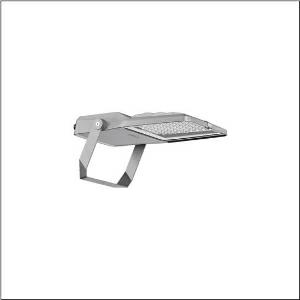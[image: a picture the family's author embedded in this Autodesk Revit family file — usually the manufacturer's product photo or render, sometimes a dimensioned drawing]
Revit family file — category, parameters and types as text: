
# Revit family: floodlight_fl_21_iq_mini___pl52_5xa7772d3d1a_25a1
name_source: partatom
category: Lighting Fixtures
units: mm (PartAtom-declared; Revit-internal decimal feet)

## family parameters
Cut with Voids When Loaded = No
Host = Face
Light Source = No
Part Type = Normal
Room Calculation Point = No
Round Connector Dimension = Use Diameter
Shared = No

## types (1)
- --- (1 x LED, 15340 lm, 143 W, 3000K)
    Apparent Load = 143 VA
    CIE Flux Codes = 26 60 98 100 100
    Color Rendering = 80
    Color Temperature = 3000K
    Default Elevation = 1800 mm
    Description = Floodlight FL 21 iQ mini, floodlight, primary light control with lens, of PMMA, primary optical cover: protective disc, of toughened safety glass, transparent, light distribution: PL52, light emission: direct distribution, installation type: surface-mounted, LED, High Power LED, rated luminous flux: 15.340lm, luminous efficacy: 107lm/W, light colour: 830, colour temperature: 3000K, control gear: iQ Street-Remote/DALI, control: Street-Remote, Auto-Match, Temp-Guard, Night-Set, Smart-Wire, Desk-Remote (wireless, voltage-free reading and setting of iQ features in the workshop via application-optimized NFC function/RFID function), optimised constant luminous flux control (CLO 2.0), with terminal, 6-pole, mains connection: 220..240V, AC, 50/60Hz, start of lifetime: 143W, end of service life: 152W, reduction: 61W, luminaire housing, of diecast aluminium, powder-coated, Siteco® metallic grey (DB 702S), corrosivity category C5 mid according to DIN EN ISO 12944, suitable for swimming pools, chlorine-resistant, sealing non-destructively replaceable, mounting bracket, of steel, galvanised, powder-coated, Siteco® metallic grey (DB 702S), protection rating (complete): IP66, insulation class (complete): insulation class II (safety insulation), certification: CE, ENEC, VDE, protection symbol: D, impact resistance: IK08, permissible operating ambient temperature: -40..+40°C, permissible operating ambient temperature for outdoor applications: -40..+50°C, standard: DIN EN 12944, LABS conformity tested according to VDMA 24364:2018-05, packaging unit: 1 piece

Light Distribution: PL52
    Height = 70 mm
    Lamp = 1 x LED
    Lamp Light Flux = 15340 lm
    Lamp Power = 143 W
    Lamp count = 1
    Length = 485 mm
    Luminous efficacy = 107 lm/W
    Manufacturer = Siteco
    ModVariant = No
    Model = 5XA7772D3D1A
    Number of Poles = 1
    OnlyDefault = Yes
    Power Factor = 1
    Product Name = Floodlight FL 21 iQ mini | PL52
    Product group = floodlight | pylon annexe
    ProductGroupID = 6200
    Protection Class = Protection class II
    Protection Degree = IP 66
    RLX_Detail_Level = 1
    RLX_Emergency_Light_Flux = 0 lm
    RLX_Emergency_Type = 0
    RLX_Emergency_Type_DB = No
    RlxData = <blob elided: 96941 chars, md5=e86fc495>
    Socket = socket
    Standby Power = 0 W
    System Light Flux = 15340 lm
    System Power = 143 W
    Type Comments = factory setting: luminous flux: 100 % | dim-lin: 254 | 730 mA
    Type Image = l_1006845.jpg
    URL = http://relux.com
    VarID = @adj_163674
    Voltage = 0 V
    Weight = 0.00 kg
    Width = 337 mm

## geometry (parser evidence)
native form markers: Blend x4, Sweep x15
no freeform markers — native parametric forms only
